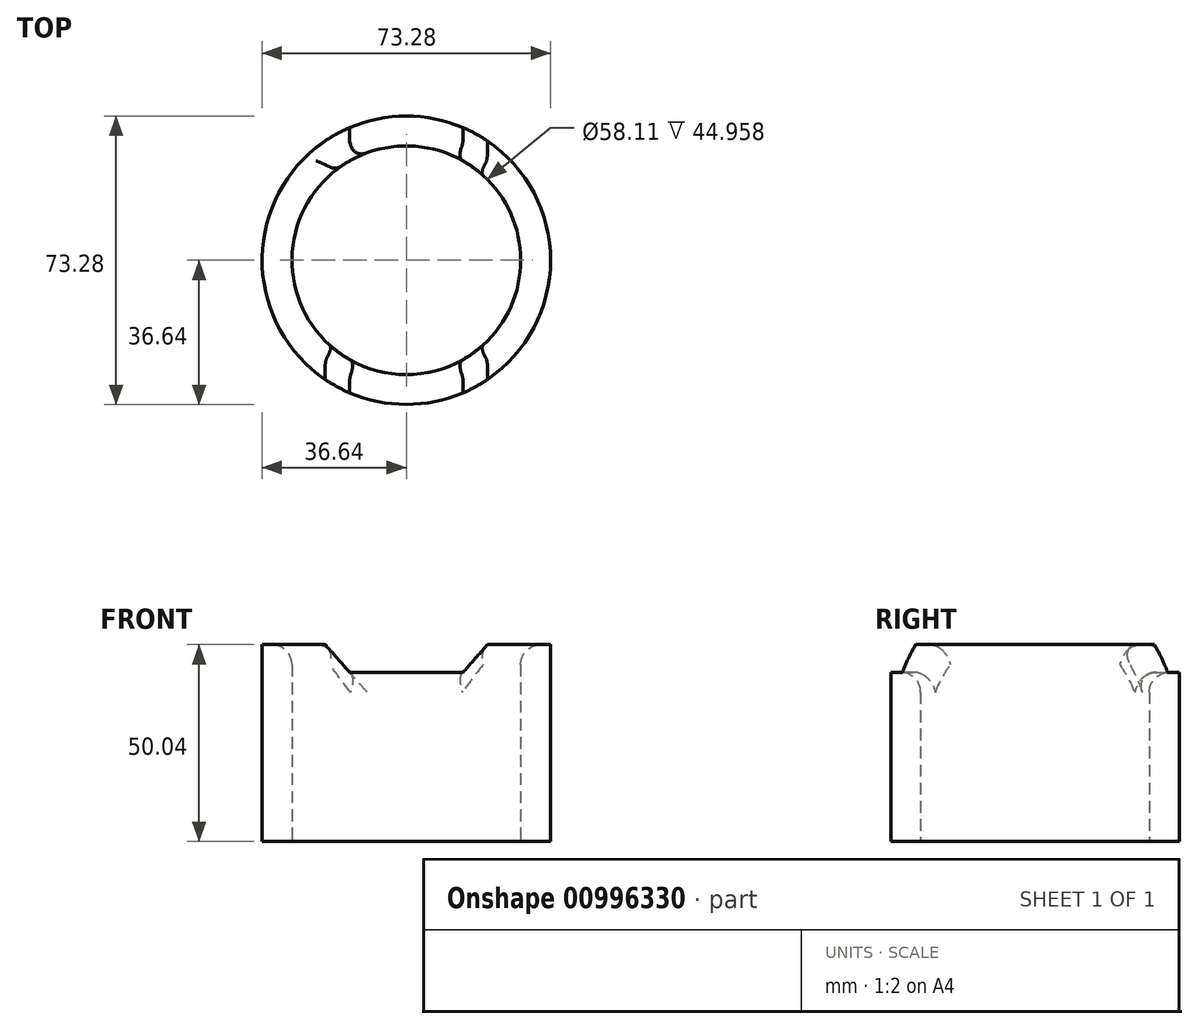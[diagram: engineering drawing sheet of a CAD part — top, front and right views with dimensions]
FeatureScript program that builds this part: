
annotation { "Feature Type Name" : "Feature", "Feature Type Description" : "" }
export const myFeature = defineFeature(function(context is Context, id is Id, definition is map)
    precondition{}
    {
        {
            var Q0;
            Q0=qCreatedBy(makeId("Top.planeOp"),FACE);
            var sketch = newSketch(context, id + "F0", { "sketchPlane" : qUnion([Q0])});
            skCircle(sketch, "E0", {"center": v(0, 0) * mm, "radius": 36.64 * mm});
            skCircle(sketch, "E1", {"center": v(0, 0) * mm, "radius": 29.05 * mm});
            skSolve(sketch);
        }
        {
            var Q0;
            Q0=makeQuery(id+"F0.imprint","IMPRINT",FACE,{"disambiguationData":[TD([[makeQuery(id+"F0.imprint","IMPRINT",EDGE,{"derivedFrom":sQuery(id+"F0.wireOp",EDGE,"E0")}),1.0]])]});
            extrude(context, id + "F1", {"entities" : qUnion([Q0]), "depth" : 50.04 * mm, "offsetDistance" : 25.4 * mm});
        }
        {
            var Q0;
            Q0=qCreatedBy(makeId("Front.planeOp"),FACE);
            var sketch = newSketch(context, id + "F2", { "sketchPlane" : qUnion([Q0])});
            skLineSegment(sketch, "E2", {"start": v(23.81, 53.66) * mm, "end": v(14.41, 42.99) * mm});
            skLineSegment(sketch, "E3", {"start": v(14.41, 42.99) * mm, "end": v(0, 42.99) * mm});
            skLineSegment(sketch, "E4.MirrorCS", {"start": v(-14.41, 42.99) * mm, "end": v(0, 42.99) * mm});
            skLineSegment(sketch, "E5.MirrorCS", {"start": v(-23.81, 53.66) * mm, "end": v(-14.41, 42.99) * mm});
            skLineSegment(sketch, "E6", {"start": v(23.81, 53.66) * mm, "end": v(-23.81, 53.66) * mm});
            skSolve(sketch);
        }
        {
            var Q0;
            Q0=makeQuery(id+"F2.imprint","IMPRINT",FACE,{"disambiguationData":[TD([[makeQuery(id+"F2.imprint","IMPRINT",EDGE,{"derivedFrom":sQuery(id+"F2.wireOp",EDGE,"E2")}),-1.0]])]});
            extrude(context, id + "F3", {"entities" : qUnion([Q0]), "operationType" : NewBodyOperationType.REMOVE, "depth" : 60.96 * mm, "offsetDistance" : 25.4 * mm, "hasSecondDirection" : true, "secondDirectionOppositeDirection" : true, "secondDirectionDepth" : 73.15 * mm});
        }
        {
            var Q0;
            Q0=makeQuery(id+"F3.boolean.opBoolean","INTERSECT",EDGE,{"disambiguationData":[OD(1.0)],"derivedFrom":[makeQuery(id+"F1.opExtrude","SWEPT_FACE",FACE,{"disambiguationData":[OSD([sQuery(id+"F0.wireOp",EDGE,"E1")])]}),makeQuery(id+"F3.opExtrude","SWEPT_FACE",FACE,{"disambiguationData":[OSD([sQuery(id+"F2.wireOp",EDGE,"E3"),sQuery(id+"F2.wireOp",EDGE,"E4.MirrorCS")])]})]});
            var Q1;
            Q1=makeQuery(id+"F3.boolean.opBoolean","INTERSECT",EDGE,{"disambiguationData":[OD(1.0)],"derivedFrom":[makeQuery(id+"F1.opExtrude","SWEPT_FACE",FACE,{"disambiguationData":[OSD([sQuery(id+"F0.wireOp",EDGE,"E1")])]}),makeQuery(id+"F3.opExtrude","SWEPT_FACE",FACE,{"disambiguationData":[OSD([sQuery(id+"F2.wireOp",EDGE,"E2")])]})]});
            var Q2;
            {var subQ0=sQuery(id+"F0.wireOp",EDGE,"E1");Q2=makeQuery(id+"F3.boolean.opBoolean","SPLIT",EDGE,{"disambiguationData":[TD([makeQuery(id+"F3.opExtrude","SWEPT_FACE",FACE,{"disambiguationData":[OSD([sQuery(id+"F2.wireOp",EDGE,"E2")])]})])],"derivedFrom":makeQuery(id+"F1.opExtrude","CAP_EDGE",EDGE,{"disambiguationData":[OSD([subQ0])],"isStart":false})});}
            var Q3;
            Q3=makeQuery(id+"F3.boolean.opBoolean","INTERSECT",EDGE,{"disambiguationData":[OD(0.0)],"derivedFrom":[makeQuery(id+"F1.opExtrude","SWEPT_FACE",FACE,{"disambiguationData":[OSD([sQuery(id+"F0.wireOp",EDGE,"E1")])]}),makeQuery(id+"F3.opExtrude","SWEPT_FACE",FACE,{"disambiguationData":[OSD([sQuery(id+"F2.wireOp",EDGE,"E2")])]})]});
            var Q4;
            Q4=makeQuery(id+"F3.boolean.opBoolean","INTERSECT",EDGE,{"disambiguationData":[OD(0.0)],"derivedFrom":[makeQuery(id+"F1.opExtrude","SWEPT_FACE",FACE,{"disambiguationData":[OSD([sQuery(id+"F0.wireOp",EDGE,"E1")])]}),makeQuery(id+"F3.opExtrude","SWEPT_FACE",FACE,{"disambiguationData":[OSD([sQuery(id+"F2.wireOp",EDGE,"E3"),sQuery(id+"F2.wireOp",EDGE,"E4.MirrorCS")])]})]});
            var Q5;
            Q5=makeQuery(id+"F3.boolean.opBoolean","INTERSECT",EDGE,{"disambiguationData":[OD(0.0)],"derivedFrom":[makeQuery(id+"F1.opExtrude","SWEPT_FACE",FACE,{"disambiguationData":[OSD([sQuery(id+"F0.wireOp",EDGE,"E1")])]}),makeQuery(id+"F3.opExtrude","SWEPT_FACE",FACE,{"disambiguationData":[OSD([sQuery(id+"F2.wireOp",EDGE,"E5.MirrorCS")])]})]});
            var Q6;
            {var subQ0=sQuery(id+"F0.wireOp",EDGE,"E1");Q6=makeQuery(id+"F3.boolean.opBoolean","SPLIT",EDGE,{"disambiguationData":[TD([makeQuery(id+"F3.opExtrude","SWEPT_FACE",FACE,{"disambiguationData":[OSD([sQuery(id+"F2.wireOp",EDGE,"E5.MirrorCS")])]})])],"derivedFrom":makeQuery(id+"F1.opExtrude","CAP_EDGE",EDGE,{"disambiguationData":[OSD([subQ0])],"isStart":false})});}
            var Q7;
            Q7=makeQuery(id+"F3.boolean.opBoolean","INTERSECT",EDGE,{"disambiguationData":[OD(1.0)],"derivedFrom":[makeQuery(id+"F1.opExtrude","CAP_FACE",FACE,{"disambiguationData":[OSD([sQuery(id+"F0.wireOp",EDGE,"E0"),sQuery(id+"F0.wireOp",EDGE,"E1")])],"isStart":false}),makeQuery(id+"F3.opExtrude","SWEPT_FACE",FACE,{"disambiguationData":[OSD([sQuery(id+"F2.wireOp",EDGE,"E5.MirrorCS")])]})]});
            fillet(context, id + "F4", {"entities" : qUnion([Q0, Q1, Q2, Q3, Q4, Q5, Q6, Q7]), "radius" : 5.08 * mm, "tangentPropagation" : true, "allowEdgeOverflow" : false});
        }
    });
